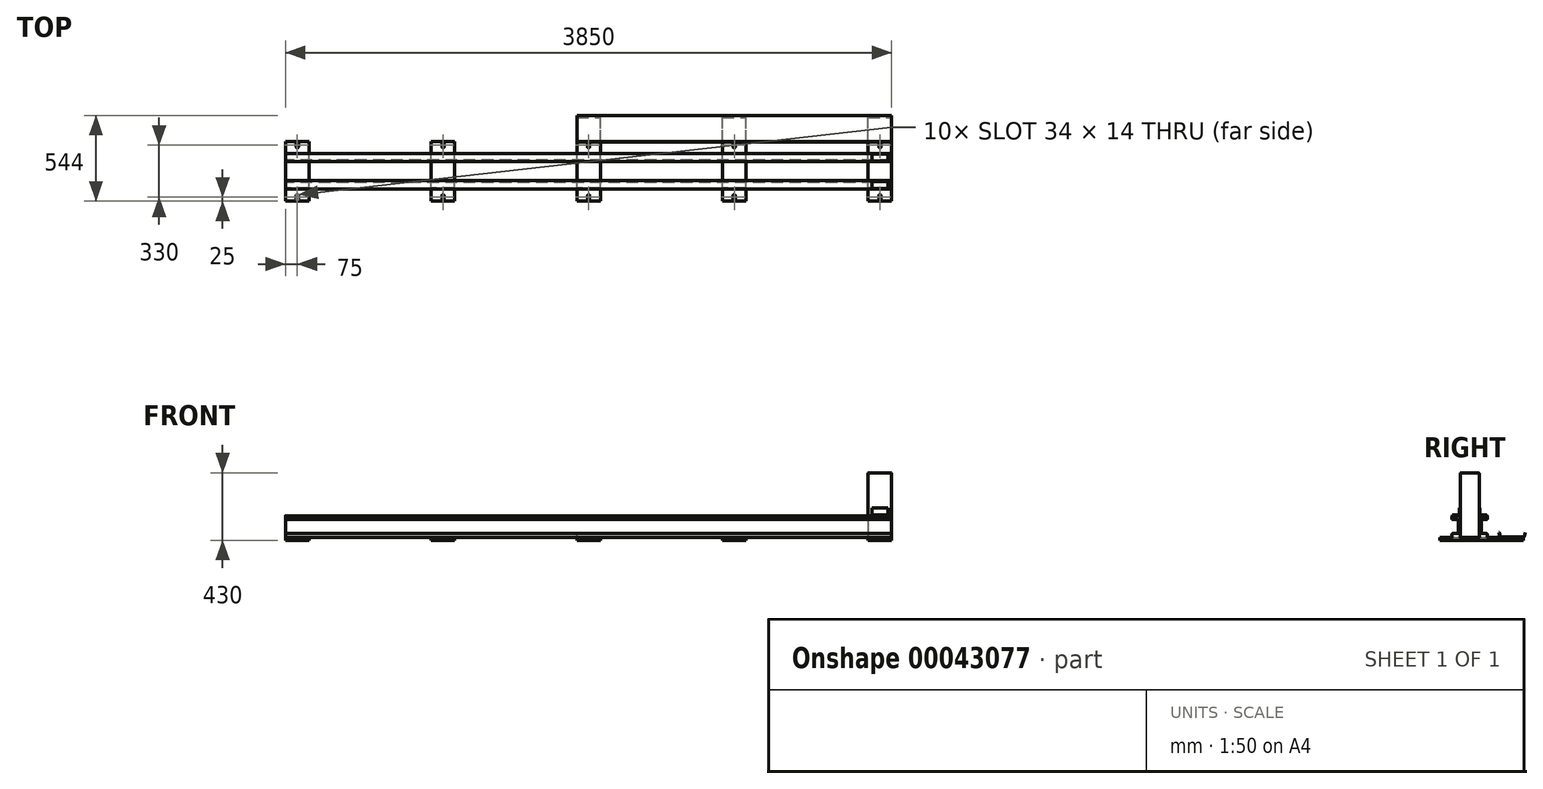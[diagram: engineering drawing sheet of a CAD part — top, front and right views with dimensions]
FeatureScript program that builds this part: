
annotation { "Feature Type Name" : "Feature", "Feature Type Description" : "" }
export const myFeature = defineFeature(function(context is Context, id is Id, definition is map)
    precondition{}
    {
        {
            var Q0;
            Q0=qCreatedBy(makeId("Top.planeOp"),FACE);
            var sketch = newSketch(context, id + "F0", { "sketchPlane" : qUnion([Q0])});
            skLineSegment(sketch, "E0.rect.bottom", {"start": v(-1925, 190) * mm, "end": v(1925, 190) * mm, "construction": true});
            skLineSegment(sketch, "E0.rect.top", {"start": v(-1925, -190) * mm, "end": v(1925, -190) * mm, "construction": true});
            skLineSegment(sketch, "E0.rect.left", {"start": v(-1925, 190) * mm, "end": v(-1925, -190) * mm, "construction": true});
            skLineSegment(sketch, "E0.rect.right", {"start": v(1925, 190) * mm, "end": v(1925, -190) * mm, "construction": true});
            skPoint(sketch, "E0.rect.middle", {"position": v(0, 0) * mm});
            skLineSegment(sketch, "E1.bottom", {"start": v(-1925, -190) * mm, "end": v(-1775, -190) * mm});
            skLineSegment(sketch, "E1.top", {"start": v(-1925, 190) * mm, "end": v(-1775, 190) * mm});
            skLineSegment(sketch, "E1.left", {"start": v(-1925, -190) * mm, "end": v(-1925, 190) * mm});
            skLineSegment(sketch, "E1.right", {"start": v(-1775, -190) * mm, "end": v(-1775, 190) * mm});
            skLineSegment(sketch, "E2", {"start": v(-1607.82, 0) * mm, "end": v(-2050.24, 0) * mm, "construction": true});
            skPoint(sketch, "E2.startSnap0", {"position": v(-1775, 0) * mm});
            skPoint(sketch, "E2.endSnap0", {"position": v(-1775, 0) * mm});
            skLineSegment(sketch, "E3", {"start": v(-1850, 190) * mm, "end": v(-1850, -266.2) * mm, "construction": true});
            skPoint(sketch, "E3.endSnap0", {"position": v(-1850, -190) * mm});
            skLineSegment(sketch, "E4.0", {"start": v(-1607.82, 155) * mm, "end": v(-2050.24, 155) * mm, "construction": true});
            skLineSegment(sketch, "E5.0", {"start": v(-1607.82, 175) * mm, "end": v(-2050.24, 175) * mm, "construction": true});
            skLineSegment(sketch, "E6", {"start": v(-1850, 175) * mm, "end": v(-1850, 155) * mm});
            skArc(sketch, "E7.0.startCap", {"start": v(-1857, 175) * mm, "mid": v(-1850, 182) * mm, "end": v(-1843, 175) * mm});
            skArc(sketch, "E7.0.endCap", {"start": v(-1843, 155) * mm, "mid": v(-1850, 148) * mm, "end": v(-1857, 155) * mm});
            skLineSegment(sketch, "E7.0.left", {"start": v(-1843, 175) * mm, "end": v(-1843, 155) * mm});
            skLineSegment(sketch, "E7.0.right", {"start": v(-1857, 175) * mm, "end": v(-1857, 155) * mm});
            skLineSegment(sketch, "E8.MirrorCS", {"start": v(-1857, -175) * mm, "end": v(-1857, -155) * mm});
            skLineSegment(sketch, "E9.MirrorCS", {"start": v(-1850, -175) * mm, "end": v(-1850, -155) * mm});
            skArc(sketch, "E10.MirrorCS", {"start": v(-1857, -175) * mm, "mid": v(-1850, -182) * mm, "end": v(-1843, -175) * mm});
            skArc(sketch, "E11.MirrorCS", {"start": v(-1843, -155) * mm, "mid": v(-1850, -148) * mm, "end": v(-1857, -155) * mm});
            skLineSegment(sketch, "E12.MirrorCS", {"start": v(-1843, -175) * mm, "end": v(-1843, -155) * mm});
            skLineSegment(sketch, "E13.1.0.0", {"start": v(-1000, -190) * mm, "end": v(-850, -190) * mm});
            skLineSegment(sketch, "E13.1.0.1", {"start": v(-1000, 190) * mm, "end": v(-850, 190) * mm});
            skPoint(sketch, "E13.1.0.2", {"position": v(-850, 0) * mm});
            skLineSegment(sketch, "E13.1.0.3", {"start": v(-1000, -190) * mm, "end": v(-1000, 190) * mm});
            skLineSegment(sketch, "E13.1.0.4", {"start": v(-850, -190) * mm, "end": v(-850, 190) * mm});
            skPoint(sketch, "E13.1.0.5", {"position": v(-925, -190) * mm});
            skLineSegment(sketch, "E13.1.0.6", {"start": v(-1000, 190) * mm, "end": v(-1000, -190) * mm, "construction": true});
            skPoint(sketch, "E13.1.0.7", {"position": v(-850, 0) * mm});
            skLineSegment(sketch, "E13.1.0.8", {"start": v(-932, -175) * mm, "end": v(-932, -155) * mm});
            skArc(sketch, "E13.1.0.9", {"start": v(-932, 175) * mm, "mid": v(-925, 182) * mm, "end": v(-918, 175) * mm});
            skArc(sketch, "E13.1.0.10", {"start": v(-932, -175) * mm, "mid": v(-925, -182) * mm, "end": v(-918, -175) * mm});
            skArc(sketch, "E13.1.0.11", {"start": v(-918, 155) * mm, "mid": v(-925, 148) * mm, "end": v(-932, 155) * mm});
            skLineSegment(sketch, "E13.1.0.12", {"start": v(-918, 175) * mm, "end": v(-918, 155) * mm});
            skLineSegment(sketch, "E13.1.0.13", {"start": v(-918, -175) * mm, "end": v(-918, -155) * mm});
            skLineSegment(sketch, "E13.1.0.14", {"start": v(-925, 175) * mm, "end": v(-925, 155) * mm});
            skLineSegment(sketch, "E13.1.0.15", {"start": v(-925, -175) * mm, "end": v(-925, -155) * mm});
            skLineSegment(sketch, "E13.1.0.16", {"start": v(-932, 175) * mm, "end": v(-932, 155) * mm});
            skArc(sketch, "E13.1.0.17", {"start": v(-918, -155) * mm, "mid": v(-925, -148) * mm, "end": v(-932, -155) * mm});
            skLineSegment(sketch, "E13.2.0.0", {"start": v(-75, -190) * mm, "end": v(75, -190) * mm});
            skPoint(sketch, "E13.2.0.2", {"position": v(75, 0) * mm});
            skLineSegment(sketch, "E13.2.0.3", {"start": v(-75, -190) * mm, "end": v(-75, 190) * mm});
            skLineSegment(sketch, "E13.2.0.4", {"start": v(75, -190) * mm, "end": v(75, 190) * mm});
            skPoint(sketch, "E13.2.0.5", {"position": v(0, -190) * mm});
            skLineSegment(sketch, "E13.2.0.6", {"start": v(-75, 190) * mm, "end": v(-75, -190) * mm, "construction": true});
            skPoint(sketch, "E13.2.0.7", {"position": v(75, 0) * mm});
            skLineSegment(sketch, "E13.2.0.8", {"start": v(-7, -175) * mm, "end": v(-7, -155) * mm});
            skArc(sketch, "E13.2.0.9", {"start": v(-7, 175) * mm, "mid": v(0, 182) * mm, "end": v(7, 175) * mm});
            skArc(sketch, "E13.2.0.10", {"start": v(-7, -175) * mm, "mid": v(0, -182) * mm, "end": v(7, -175) * mm});
            skArc(sketch, "E13.2.0.11", {"start": v(7, 155) * mm, "mid": v(0, 148) * mm, "end": v(-7, 155) * mm});
            skLineSegment(sketch, "E13.2.0.12", {"start": v(7, 175) * mm, "end": v(7, 155) * mm});
            skLineSegment(sketch, "E13.2.0.13", {"start": v(7, -175) * mm, "end": v(7, -155) * mm});
            skLineSegment(sketch, "E13.2.0.14", {"start": v(0, 175) * mm, "end": v(0, 155) * mm});
            skLineSegment(sketch, "E13.2.0.15", {"start": v(0, -175) * mm, "end": v(0, -155) * mm});
            skLineSegment(sketch, "E13.2.0.16", {"start": v(-7, 175) * mm, "end": v(-7, 155) * mm});
            skArc(sketch, "E13.2.0.17", {"start": v(7, -155) * mm, "mid": v(0, -148) * mm, "end": v(-7, -155) * mm});
            skLineSegment(sketch, "E13.3.0.0", {"start": v(850, -190) * mm, "end": v(1000, -190) * mm});
            skPoint(sketch, "E13.3.0.2", {"position": v(1000, 0) * mm});
            skLineSegment(sketch, "E13.3.0.3", {"start": v(850, -190) * mm, "end": v(850, 190) * mm});
            skLineSegment(sketch, "E13.3.0.4", {"start": v(1000, -190) * mm, "end": v(1000, 190) * mm});
            skPoint(sketch, "E13.3.0.5", {"position": v(925, -190) * mm});
            skLineSegment(sketch, "E13.3.0.6", {"start": v(850, 190) * mm, "end": v(850, -190) * mm, "construction": true});
            skPoint(sketch, "E13.3.0.7", {"position": v(1000, 0) * mm});
            skLineSegment(sketch, "E13.3.0.8", {"start": v(918, -175) * mm, "end": v(918, -155) * mm});
            skArc(sketch, "E13.3.0.9", {"start": v(918, 175) * mm, "mid": v(925, 182) * mm, "end": v(932, 175) * mm});
            skArc(sketch, "E13.3.0.10", {"start": v(918, -175) * mm, "mid": v(925, -182) * mm, "end": v(932, -175) * mm});
            skArc(sketch, "E13.3.0.11", {"start": v(932, 155) * mm, "mid": v(925, 148) * mm, "end": v(918, 155) * mm});
            skLineSegment(sketch, "E13.3.0.12", {"start": v(932, 175) * mm, "end": v(932, 155) * mm});
            skLineSegment(sketch, "E13.3.0.13", {"start": v(932, -175) * mm, "end": v(932, -155) * mm});
            skLineSegment(sketch, "E13.3.0.14", {"start": v(925, 175) * mm, "end": v(925, 155) * mm});
            skLineSegment(sketch, "E13.3.0.15", {"start": v(925, -175) * mm, "end": v(925, -155) * mm});
            skLineSegment(sketch, "E13.3.0.16", {"start": v(918, 175) * mm, "end": v(918, 155) * mm});
            skArc(sketch, "E13.3.0.17", {"start": v(932, -155) * mm, "mid": v(925, -148) * mm, "end": v(918, -155) * mm});
            skLineSegment(sketch, "E13.4.0.0", {"start": v(1775, -190) * mm, "end": v(1925, -190) * mm});
            skPoint(sketch, "E13.4.0.2", {"position": v(1925, 0) * mm});
            skLineSegment(sketch, "E13.4.0.3", {"start": v(1775, -190) * mm, "end": v(1775, 190) * mm});
            skLineSegment(sketch, "E13.4.0.4", {"start": v(1925, -190) * mm, "end": v(1925, 190) * mm});
            skPoint(sketch, "E13.4.0.5", {"position": v(1850, -190) * mm});
            skLineSegment(sketch, "E13.4.0.6", {"start": v(1775, 190) * mm, "end": v(1775, -190) * mm, "construction": true});
            skPoint(sketch, "E13.4.0.7", {"position": v(1925, 0) * mm});
            skLineSegment(sketch, "E13.4.0.8", {"start": v(1843, -175) * mm, "end": v(1843, -155) * mm});
            skArc(sketch, "E13.4.0.9", {"start": v(1843, 175) * mm, "mid": v(1850, 182) * mm, "end": v(1857, 175) * mm});
            skArc(sketch, "E13.4.0.10", {"start": v(1843, -175) * mm, "mid": v(1850, -182) * mm, "end": v(1857, -175) * mm});
            skArc(sketch, "E13.4.0.11", {"start": v(1857, 155) * mm, "mid": v(1850, 148) * mm, "end": v(1843, 155) * mm});
            skLineSegment(sketch, "E13.4.0.12", {"start": v(1857, 175) * mm, "end": v(1857, 155) * mm});
            skLineSegment(sketch, "E13.4.0.13", {"start": v(1857, -175) * mm, "end": v(1857, -155) * mm});
            skLineSegment(sketch, "E13.4.0.14", {"start": v(1850, 175) * mm, "end": v(1850, 155) * mm});
            skLineSegment(sketch, "E13.4.0.15", {"start": v(1850, -175) * mm, "end": v(1850, -155) * mm});
            skLineSegment(sketch, "E13.4.0.16", {"start": v(1843, 175) * mm, "end": v(1843, 155) * mm});
            skArc(sketch, "E13.4.0.17", {"start": v(1857, -155) * mm, "mid": v(1850, -148) * mm, "end": v(1843, -155) * mm});
            skLineSegment(sketch, "E13.direction1", {"start": v(-1925, -190) * mm, "end": v(-1000, -190) * mm, "construction": true});
            skLineSegment(sketch, "E14.top", {"start": v(-75, 340) * mm, "end": v(75, 340) * mm});
            skLineSegment(sketch, "E14.left", {"start": v(-75, -190) * mm, "end": v(-75, 340) * mm});
            skLineSegment(sketch, "E14.right", {"start": v(75, -190) * mm, "end": v(75, 340) * mm});
            skLineSegment(sketch, "E15.1.0.0", {"start": v(850, 340) * mm, "end": v(1000, 340) * mm});
            skLineSegment(sketch, "E15.1.0.1", {"start": v(1000, -190) * mm, "end": v(1000, 340) * mm});
            skLineSegment(sketch, "E15.1.0.2", {"start": v(850, -190) * mm, "end": v(850, 340) * mm});
            skLineSegment(sketch, "E15.2.0.0", {"start": v(1775, 340) * mm, "end": v(1925, 340) * mm});
            skLineSegment(sketch, "E15.2.0.1", {"start": v(1925, -190) * mm, "end": v(1925, 340) * mm});
            skLineSegment(sketch, "E15.2.0.2", {"start": v(1775, -190) * mm, "end": v(1775, 340) * mm});
            skLineSegment(sketch, "E15.direction1", {"start": v(-75, 340) * mm, "end": v(850, 340) * mm, "construction": true});
            skSolve(sketch);
        }
        {
            var Q0;
            Q0 = qSketchRegion(id + "F0", true);
            extrude(context, id + "F1", {"entities" : qUnion([Q0]), "oppositeDirection" : true, "depth" : 20 * mm});
        }
        {
            var Q0;
            Q0=qCreatedBy(makeId("Right.planeOp"),FACE);
            var sketch = newSketch(context, id + "F2", { "sketchPlane" : qUnion([Q0])});
            skLineSegment(sketch, "E16", {"start": v(0, 0) * mm, "end": v(0, 313.62) * mm, "construction": true});
            skLineSegment(sketch, "E17.0", {"start": v(-113, 0) * mm, "end": v(-113, 313.62) * mm, "construction": true});
            skLineSegment(sketch, "E18.bottom", {"start": v(-108, 0) * mm, "end": v(-65, 0) * mm});
            skLineSegment(sketch, "E18.top", {"start": v(-108, 135.5) * mm, "end": v(-65, 135.5) * mm});
            skLineSegment(sketch, "E18.left", {"start": v(-113, 5) * mm, "end": v(-113, 18) * mm});
            skLineSegment(sketch, "E18.right", {"start": v(-60, 5) * mm, "end": v(-60, 130.5) * mm});
            skLineSegment(sketch, "E19.rect.bottom", {"start": v(-108, 112.5) * mm, "end": v(-77.5, 112.5) * mm});
            skLineSegment(sketch, "E19.rect.top", {"start": v(-108, 23) * mm, "end": v(-77.5, 23) * mm});
            skLineSegment(sketch, "E19.rect.right", {"start": v(-72.5, 107.5) * mm, "end": v(-72.5, 28) * mm});
            skPoint(sketch, "E19.rect.middle", {"position": v(-113, 67.75) * mm});
            skPoint(sketch, "E19.rect.left.start.orphan", {"position": v(-153.5, 112.5) * mm});
            skPoint(sketch, "E20.orphan", {"position": v(-153.5, 23) * mm});
            skLineSegment(sketch, "E21.trimOffspring", {"start": v(-113, 117.5) * mm, "end": v(-113, 130.5) * mm});
            skPoint(sketch, "E22.visualSharp", {"position": v(-113, 135.5) * mm});
            skArc(sketch, "E22.filletArc", {"start": v(-108, 135.5) * mm, "mid": v(-111.54, 134.04) * mm, "end": v(-113, 130.5) * mm});
            skPoint(sketch, "E23.visualSharp", {"position": v(-113, 0) * mm});
            skArc(sketch, "E23.filletArc", {"start": v(-113, 5) * mm, "mid": v(-111.54, 1.46) * mm, "end": v(-108, 0) * mm});
            skPoint(sketch, "E24.visualSharp", {"position": v(-60, 135.5) * mm});
            skArc(sketch, "E24.filletArc", {"start": v(-60, 130.5) * mm, "mid": v(-61.46, 134.04) * mm, "end": v(-65, 135.5) * mm});
            skPoint(sketch, "E25.visualSharp", {"position": v(-60, 0) * mm});
            skArc(sketch, "E25.filletArc", {"start": v(-65, 0) * mm, "mid": v(-61.46, 1.46) * mm, "end": v(-60, 5) * mm});
            skPoint(sketch, "E26.visualSharp", {"position": v(-72.5, 23) * mm});
            skArc(sketch, "E26.filletArc", {"start": v(-77.5, 23) * mm, "mid": v(-73.96, 24.46) * mm, "end": v(-72.5, 28) * mm});
            skPoint(sketch, "E27.visualSharp", {"position": v(-72.5, 112.5) * mm});
            skArc(sketch, "E27.filletArc", {"start": v(-72.5, 107.5) * mm, "mid": v(-73.96, 111.04) * mm, "end": v(-77.5, 112.5) * mm});
            skPoint(sketch, "E28.visualSharp", {"position": v(-113, 112.5) * mm});
            skArc(sketch, "E28.filletArc", {"start": v(-113, 117.5) * mm, "mid": v(-111.54, 113.96) * mm, "end": v(-108, 112.5) * mm});
            skPoint(sketch, "E29.visualSharp", {"position": v(-113, 23) * mm});
            skArc(sketch, "E29.filletArc", {"start": v(-108, 23) * mm, "mid": v(-111.54, 21.54) * mm, "end": v(-113, 18) * mm});
            skArc(sketch, "E30.MirrorCS", {"start": v(60, 130.5) * mm, "mid": v(61.46, 134.04) * mm, "end": v(65, 135.5) * mm});
            skLineSegment(sketch, "E31.MirrorCS", {"start": v(113, 5) * mm, "end": v(113, 18) * mm});
            skLineSegment(sketch, "E32.MirrorCS", {"start": v(113, 117.5) * mm, "end": v(113, 130.5) * mm});
            skArc(sketch, "E33.MirrorCS", {"start": v(108, 135.5) * mm, "mid": v(111.54, 134.04) * mm, "end": v(113, 130.5) * mm});
            skArc(sketch, "E34.MirrorCS", {"start": v(113, 5) * mm, "mid": v(111.54, 1.46) * mm, "end": v(108, 0) * mm});
            skArc(sketch, "E35.MirrorCS", {"start": v(72.5, 107.5) * mm, "mid": v(73.96, 111.04) * mm, "end": v(77.5, 112.5) * mm});
            skArc(sketch, "E36.MirrorCS", {"start": v(77.5, 23) * mm, "mid": v(73.96, 24.46) * mm, "end": v(72.5, 28) * mm});
            skArc(sketch, "E37.MirrorCS", {"start": v(65, 0) * mm, "mid": v(61.46, 1.46) * mm, "end": v(60, 5) * mm});
            skArc(sketch, "E38.MirrorCS", {"start": v(113, 117.5) * mm, "mid": v(111.54, 113.96) * mm, "end": v(108, 112.5) * mm});
            skArc(sketch, "E39.MirrorCS", {"start": v(108, 23) * mm, "mid": v(111.54, 21.54) * mm, "end": v(113, 18) * mm});
            skPoint(sketch, "E40.MirrorP", {"position": v(60, 135.5) * mm});
            skLineSegment(sketch, "E41.MirrorCS", {"start": v(108, 112.5) * mm, "end": v(77.5, 112.5) * mm});
            skLineSegment(sketch, "E42.MirrorCS", {"start": v(60, 5) * mm, "end": v(60, 130.5) * mm});
            skLineSegment(sketch, "E43.MirrorCS", {"start": v(108, 23) * mm, "end": v(77.5, 23) * mm});
            skLineSegment(sketch, "E44.MirrorCS", {"start": v(72.5, 107.5) * mm, "end": v(72.5, 28) * mm});
            skLineSegment(sketch, "E45.MirrorCS", {"start": v(108, 135.5) * mm, "end": v(65, 135.5) * mm});
            skLineSegment(sketch, "E46.MirrorCS", {"start": v(108, 0) * mm, "end": v(65, 0) * mm});
            skPoint(sketch, "E47.MirrorP", {"position": v(113, 67.75) * mm});
            skPoint(sketch, "E48.MirrorP", {"position": v(113, 0) * mm});
            skPoint(sketch, "E49.MirrorP", {"position": v(72.5, 23) * mm});
            skPoint(sketch, "E50.MirrorP", {"position": v(72.5, 112.5) * mm});
            skPoint(sketch, "E51.MirrorP", {"position": v(113, 135.5) * mm});
            skPoint(sketch, "E52.MirrorP", {"position": v(60, 0) * mm});
            skPoint(sketch, "E53.MirrorP", {"position": v(113, 23) * mm});
            skPoint(sketch, "E54.MirrorP", {"position": v(113, 112.5) * mm});
            skSolve(sketch);
        }
        {
            var Q0;
            Q0 = qSketchRegion(id + "F2", true);
            extrude(context, id + "F3", {"entities" : qUnion([Q0]), "operationType" : NewBodyOperationType.ADD, "endBound" : BoundingType.SYMMETRIC, "depth" : 3850 * mm});
        }
        {
            var Q0;
            Q0=makeQuery(id+"F1.opExtrude","SWEPT_FACE",FACE,{"disambiguationData":[OSD([sQuery(id+"F0.wireOp",EDGE,"E15.2.0.1")])]});
            var sketch = newSketch(context, id + "F4", { "sketchPlane" : qUnion([Q0])});
            skLineSegment(sketch, "E55.0", {"start": v(-190, -20) * mm, "end": v(-190, 0) * mm, "construction": true});
            skLineSegment(sketch, "E56.0", {"start": v(354, -20) * mm, "end": v(354, 30) * mm, "construction": true});
            skLineSegment(sketch, "E57.0", {"start": v(346.5, -20) * mm, "end": v(346.5, 0) * mm, "construction": true});
            skLineSegment(sketch, "E58.0", {"start": v(269.5, -20) * mm, "end": v(269.5, 0) * mm, "construction": true});
            skLineSegment(sketch, "E59", {"start": v(354, 30) * mm, "end": v(347.83, 5.3) * mm});
            skLineSegment(sketch, "E60", {"start": v(341.03, 0) * mm, "end": v(269.5, 0) * mm});
            skLineSegment(sketch, "E61.0", {"start": v(341.03, 2) * mm, "end": v(269.5, 2) * mm});
            skLineSegment(sketch, "E61.1", {"start": v(352.06, 30.49) * mm, "end": v(345.89, 5.79) * mm});
            skLineSegment(sketch, "E62", {"start": v(352.06, 30.49) * mm, "end": v(354, 30) * mm});
            skLineSegment(sketch, "E63.MirrorCS", {"start": v(197.97, 0) * mm, "end": v(269.5, 0) * mm});
            skLineSegment(sketch, "E64.MirrorCS", {"start": v(197.97, 2) * mm, "end": v(269.5, 2) * mm});
            skLineSegment(sketch, "E65.MirrorCS", {"start": v(186.94, 30.49) * mm, "end": v(193.11, 5.79) * mm});
            skLineSegment(sketch, "E66.MirrorCS", {"start": v(185, 30) * mm, "end": v(191.17, 5.3) * mm});
            skLineSegment(sketch, "E67.MirrorCS", {"start": v(186.94, 30.49) * mm, "end": v(185, 30) * mm});
            skPoint(sketch, "E68.visualSharp", {"position": v(344.94, 2) * mm});
            skArc(sketch, "E68.filletArc", {"start": v(341.03, 2) * mm, "mid": v(344.11, 3.06) * mm, "end": v(345.89, 5.79) * mm});
            skPoint(sketch, "E69.visualSharp", {"position": v(194.06, 2) * mm});
            skArc(sketch, "E69.filletArc", {"start": v(193.11, 5.79) * mm, "mid": v(194.89, 3.06) * mm, "end": v(197.97, 2) * mm});
            skPoint(sketch, "E70.visualSharp", {"position": v(346.5, 0) * mm});
            skArc(sketch, "E70.filletArc", {"start": v(341.03, 0) * mm, "mid": v(345.34, 1.48) * mm, "end": v(347.83, 5.3) * mm});
            skPoint(sketch, "E71.visualSharp", {"position": v(192.5, 0) * mm});
            skArc(sketch, "E71.filletArc", {"start": v(191.17, 5.3) * mm, "mid": v(193.66, 1.48) * mm, "end": v(197.97, 0) * mm});
            skSolve(sketch);
        }
        {
            var Q0;
            Q0 = qSketchRegion(id + "F4", true);
            var Q1;
            Q1=makeQuery(id+"F1.opExtrude","SWEPT_FACE",FACE,{"disambiguationData":[OSD([sQuery(id+"F0.wireOp",EDGE,"E14.left")])]});
            extrude(context, id + "F5", {"entities" : qUnion([Q0]), "endBound" : BoundingType.UP_TO_SURFACE, "oppositeDirection" : true, "endBoundEntityFace" : qUnion([Q1]), "depth" : 25 * mm});
        }
        {
            var Q0;
            Q0=makeQuery(id+"F1.opExtrude","CAP_FACE",FACE,{"disambiguationData":[OSD([sQuery(id+"F0.wireOp",EDGE,"E13.4.0.0"),sQuery(id+"F0.wireOp",EDGE,"E13.4.0.8"),sQuery(id+"F0.wireOp",EDGE,"E13.4.0.9"),sQuery(id+"F0.wireOp",EDGE,"E13.4.0.10"),sQuery(id+"F0.wireOp",EDGE,"E13.4.0.11"),sQuery(id+"F0.wireOp",EDGE,"E13.4.0.12"),sQuery(id+"F0.wireOp",EDGE,"E13.4.0.13"),sQuery(id+"F0.wireOp",EDGE,"E13.4.0.16"),sQuery(id+"F0.wireOp",EDGE,"E13.4.0.17"),sQuery(id+"F0.wireOp",EDGE,"E15.2.0.0"),sQuery(id+"F0.wireOp",EDGE,"E15.2.0.1"),sQuery(id+"F0.wireOp",EDGE,"E15.2.0.2")])],"isStart":true});
            var sketch = newSketch(context, id + "F6", { "sketchPlane" : qUnion([Q0])});
            skLineSegment(sketch, "E72.0", {"start": v(1925, 60) * mm, "end": v(-1925, 60) * mm});
            skLineSegment(sketch, "E73.0", {"start": v(1925, -60) * mm, "end": v(-1925, -60) * mm});
            skLineSegment(sketch, "E74.0", {"start": v(1925, -190) * mm, "end": v(1925, 340) * mm});
            skLineSegment(sketch, "E75.0", {"start": v(1775, -190) * mm, "end": v(1775, 340) * mm});
            skSolve(sketch);
        }
        {
            var Q0;
            Q0 = qSketchRegion(id + "F6", true);
            extrude(context, id + "F7", {"entities" : qUnion([Q0]), "depth" : 410 * mm});
        }
        {
            var Q0;
            Q0=makeQuery(id+"F7.opExtrude","SWEPT_EDGE",EDGE,{"disambiguationData":[OSD([sQuery(id+"F6.wireOp",EDGE,"E73.0"),sQuery(id+"F6.wireOp",EDGE,"E74.0")])]});
            var Q1;
            Q1=makeQuery(id+"F7.opExtrude","SWEPT_EDGE",EDGE,{"disambiguationData":[OSD([sQuery(id+"F6.wireOp",EDGE,"E73.0"),sQuery(id+"F6.wireOp",EDGE,"E75.0")])]});
            var Q2;
            Q2=makeQuery(id+"F7.opExtrude","SWEPT_EDGE",EDGE,{"disambiguationData":[OSD([sQuery(id+"F6.wireOp",EDGE,"E72.0"),sQuery(id+"F6.wireOp",EDGE,"E74.0")])]});
            var Q3;
            Q3=makeQuery(id+"F7.opExtrude","SWEPT_EDGE",EDGE,{"disambiguationData":[OSD([sQuery(id+"F6.wireOp",EDGE,"E72.0"),sQuery(id+"F6.wireOp",EDGE,"E75.0")])]});
            var Q4;
            Q4=makeQuery(id+"F7.opExtrude","CAP_FACE",FACE,{"disambiguationData":[OSD([sQuery(id+"F6.wireOp",EDGE,"E72.0"),sQuery(id+"F6.wireOp",EDGE,"E73.0"),sQuery(id+"F6.wireOp",EDGE,"E74.0"),sQuery(id+"F6.wireOp",EDGE,"E75.0")])],"isStart":false});
            fillet(context, id + "F8", {"entities" : qUnion([Q0, Q1, Q2, Q3, Q4]), "radius" : 5 * mm, "tangentPropagation" : true, "allowEdgeOverflow" : false});
        }
        {
            var Q0;
            Q0=makeQuery(id+"F7.opExtrude","SWEPT_FACE",FACE,{"disambiguationData":[OSD([sQuery(id+"F6.wireOp",EDGE,"E74.0")])]});
            fillet(context, id + "F9", {"entities" : qUnion([Q0]), "radius" : 5 * mm, "tangentPropagation" : true, "allowEdgeOverflow" : false});
        }
        {
            var Q0;
            Q0=makeQuery(id+"F7.opExtrude","SWEPT_FACE",FACE,{"disambiguationData":[OSD([sQuery(id+"F6.wireOp",EDGE,"E74.0")])]});
            cPlane(context, id + "F10", {"entities" : qUnion([Q0]), "cplaneType" : CPlaneType.OFFSET, "offset" : 75 * mm, "oppositeDirection" : true, "width" : 150 * mm, "height" : 150 * mm});
        }
        {
            var Q0;
            Q0=qCreatedBy(id+"F10.planeOp",FACE);
            var sketch = newSketch(context, id + "F11", { "sketchPlane" : qUnion([Q0])});
            skLineSegment(sketch, "E76.0", {"start": v(-60, 5) * mm, "end": v(-60, 405) * mm});
            skLineSegment(sketch, "E77.0", {"start": v(-108, 135.5) * mm, "end": v(-63.62, 135.5) * mm});
            skPoint(sketch, "E78.orphan", {"position": v(-65, 135.5) * mm});
            skLineSegment(sketch, "E79.bottom", {"start": v(-60, 135.5) * mm, "end": v(-110, 135.5) * mm});
            skLineSegment(sketch, "E79.top", {"start": v(-60, 185.5) * mm, "end": v(-65, 185.5) * mm});
            skLineSegment(sketch, "E79.left", {"start": v(-60, 135.5) * mm, "end": v(-60, 185.5) * mm});
            skLineSegment(sketch, "E79.right", {"start": v(-110, 135.5) * mm, "end": v(-110, 185.5) * mm});
            skLineSegment(sketch, "E80.top", {"start": v(-110, 140.5) * mm, "end": v(-70, 140.5) * mm});
            skLineSegment(sketch, "E80.right", {"start": v(-65, 185.5) * mm, "end": v(-65, 145.5) * mm});
            skPoint(sketch, "E81.visualSharp", {"position": v(-65, 140.5) * mm});
            skArc(sketch, "E81.filletArc", {"start": v(-70, 140.5) * mm, "mid": v(-66.46, 141.96) * mm, "end": v(-65, 145.5) * mm});
            skSolve(sketch);
        }
        {
            var Q0;
            Q0 = qSketchRegion(id + "F11", true);
            extrude(context, id + "F12", {"entities" : qUnion([Q0]), "endBound" : BoundingType.SYMMETRIC, "depth" : 100 * mm});
        }
        {
            var Q0;
            Q0=makeQuery(id+"F12.opExtrude","SWEPT_BODY",BODY,{"disambiguationData":[OSD([sQuery(id+"F11.wireOp",EDGE,"E79.bottom"),sQuery(id+"F11.wireOp",EDGE,"E79.top"),sQuery(id+"F11.wireOp",EDGE,"E79.left"),sQuery(id+"F11.wireOp",EDGE,"E79.right"),sQuery(id+"F11.wireOp",EDGE,"E80.top"),sQuery(id+"F11.wireOp",EDGE,"E80.right"),sQuery(id+"F11.wireOp",EDGE,"E81.filletArc")])]});
            var Q1;
            Q1=qCreatedBy(makeId("Front.planeOp"),FACE);
            mirror(context, id + "F13", {"entities" : qUnion([Q0]), "mirrorPlane" : qUnion([Q1])});
        }
    });
